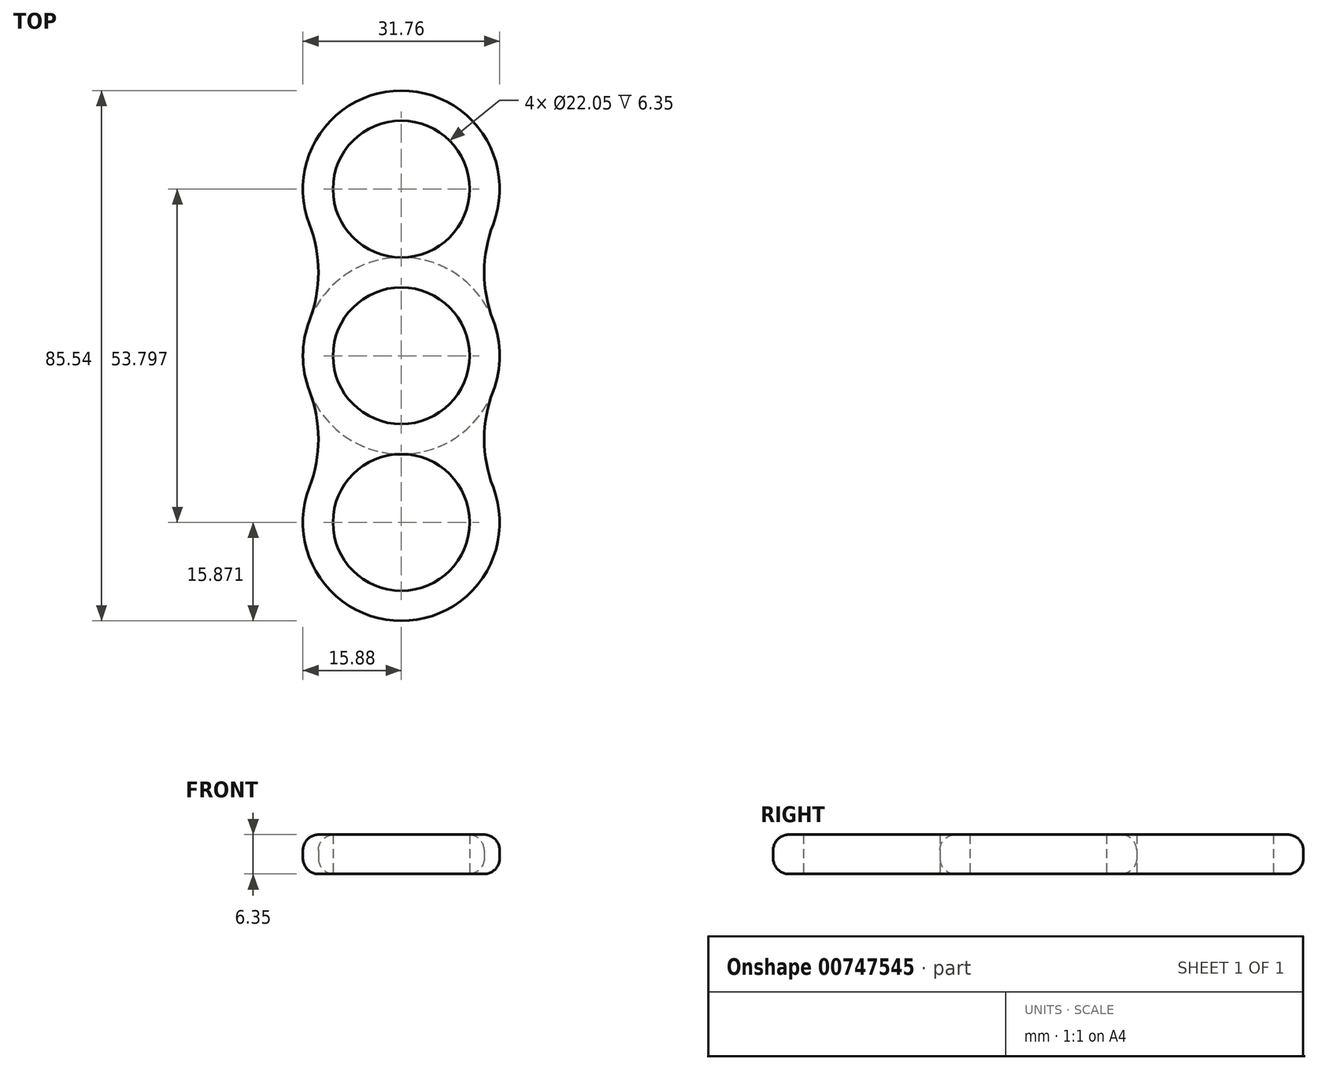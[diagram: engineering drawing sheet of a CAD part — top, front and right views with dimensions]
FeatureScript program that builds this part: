
annotation { "Feature Type Name" : "Feature", "Feature Type Description" : "" }
export const myFeature = defineFeature(function(context is Context, id is Id, definition is map)
    precondition{}
    {
        {
            var Q0;
            Q0=qCreatedBy(makeId("Top.planeOp"),FACE);
            var sketch = newSketch(context, id + "F0", { "sketchPlane" : qUnion([Q0])});
            skCircle(sketch, "E0", {"center": v(0, 0) * mm, "radius": 11.02 * mm});
            skCircle(sketch, "E1", {"center": v(0, 0) * mm, "radius": 15.88 * mm});
            skCircle(sketch, "E2", {"center": v(0, 26.9) * mm, "radius": 11.02 * mm});
            skCircle(sketch, "E3", {"center": v(0, 26.9) * mm, "radius": 15.88 * mm});
            skLineSegment(sketch, "E4", {"start": v(0, 26.9) * mm, "end": v(15.88, 26.9) * mm});
            skLineSegment(sketch, "E5", {"start": v(0, 0) * mm, "end": v(15.88, 0) * mm});
            skLineSegment(sketch, "E6", {"start": v(15.88, 0) * mm, "end": v(15.88, 26.9) * mm});
            skLineSegment(sketch, "E7", {"start": v(0, 0) * mm, "end": v(-15.88, 0) * mm});
            skLineSegment(sketch, "E8", {"start": v(-15.88, 0) * mm, "end": v(-15.88, 26.9) * mm});
            skLineSegment(sketch, "E9", {"start": v(-15.88, 26.9) * mm, "end": v(0, 26.9) * mm});
            skCircle(sketch, "E10", {"center": v(-34.97, 13.45) * mm, "radius": 21.59 * mm});
            skCircle(sketch, "E11", {"center": v(34.97, 13.45) * mm, "radius": 21.59 * mm});
            skSolve(sketch);
        }
        {
            var Q0;
            {var subQ0=sQuery(id+"F0.wireOp",EDGE,"E9");var subQ1=sQuery(id+"F0.wireOp",EDGE,"E2");var subQ2=makeQuery(id+"F0.imprint","INTERSECT",VERTEX,{"derivedFrom":[subQ1,subQ0]});Q0=makeQuery(id+"F0.imprint","IMPRINT",FACE,{"disambiguationData":[TD([[makeQuery(id+"F0.imprint","IMPRINT",EDGE,{"disambiguationData":[TD([[subQ2,1.0]])],"derivedFrom":subQ1}),-1.0]])]});}
            var Q1;
            {var subQ1=sQuery(id+"F0.wireOp",EDGE,"E3");var subQ4=sQuery(id+"F0.wireOp",EDGE,"E1");var subQ5=makeQuery(id+"F0.imprint","INTERSECT",VERTEX,{"disambiguationData":[OD(0.0)],"derivedFrom":[subQ4,subQ1]});Q1=makeQuery(id+"F0.imprint","IMPRINT",FACE,{"disambiguationData":[TD([[makeQuery(id+"F0.imprint","IMPRINT",EDGE,{"disambiguationData":[TD([[subQ5,-1.0]])],"derivedFrom":subQ4}),-1.0]])]});}
            var Q2;
            {var subQ1=sQuery(id+"F0.wireOp",EDGE,"E1");var subQ6=sQuery(id+"F0.wireOp",EDGE,"E2");var subQ7=makeQuery(id+"F0.imprint","INTERSECT",VERTEX,{"derivedFrom":[subQ1,subQ6]});Q2=makeQuery(id+"F0.imprint","IMPRINT",FACE,{"disambiguationData":[TD([[makeQuery(id+"F0.imprint","IMPRINT",EDGE,{"disambiguationData":[TD([[subQ7,-1.0]])],"derivedFrom":subQ1}),-1.0]])]});}
            var Q3;
            {var subQ0=sQuery(id+"F0.wireOp",EDGE,"E3");var subQ1=sQuery(id+"F0.wireOp",EDGE,"E1");var subQ2=makeQuery(id+"F0.imprint","INTERSECT",VERTEX,{"disambiguationData":[OD(0.0)],"derivedFrom":[subQ1,subQ0]});Q3=makeQuery(id+"F0.imprint","IMPRINT",FACE,{"disambiguationData":[TD([[makeQuery(id+"F0.imprint","IMPRINT",EDGE,{"disambiguationData":[TD([[subQ2,-1.0]])],"derivedFrom":subQ1}),1.0]])]});}
            var Q4;
            {var subQ0=sQuery(id+"F0.wireOp",EDGE,"E3");var subQ1=sQuery(id+"F0.wireOp",EDGE,"E0");var subQ2=makeQuery(id+"F0.imprint","INTERSECT",VERTEX,{"derivedFrom":[subQ1,subQ0]});Q4=makeQuery(id+"F0.imprint","IMPRINT",FACE,{"disambiguationData":[TD([[makeQuery(id+"F0.imprint","IMPRINT",EDGE,{"disambiguationData":[TD([[subQ2,1.0]])],"derivedFrom":subQ1}),-1.0]])]});}
            var Q5;
            {var subQ4=sQuery(id+"F0.wireOp",EDGE,"E3");var subQ6=sQuery(id+"F0.wireOp",EDGE,"E0");var subQ7=makeQuery(id+"F0.imprint","INTERSECT",VERTEX,{"derivedFrom":[subQ6,subQ4]});Q5=makeQuery(id+"F0.imprint","IMPRINT",FACE,{"disambiguationData":[TD([[makeQuery(id+"F0.imprint","IMPRINT",EDGE,{"disambiguationData":[TD([[subQ7,-1.0]])],"derivedFrom":subQ6}),-1.0]])]});}
            var Q6;
            {var subQ0=sQuery(id+"F0.wireOp",EDGE,"E5");var subQ1=sQuery(id+"F0.wireOp",EDGE,"E0");var subQ2=makeQuery(id+"F0.imprint","INTERSECT",VERTEX,{"derivedFrom":[subQ1,subQ0]});Q6=makeQuery(id+"F0.imprint","IMPRINT",FACE,{"disambiguationData":[TD([[makeQuery(id+"F0.imprint","IMPRINT",EDGE,{"disambiguationData":[TD([[subQ2,1.0]])],"derivedFrom":subQ1}),-1.0]])]});}
            var Q7;
            {var subQ0=sQuery(id+"F0.wireOp",EDGE,"E11");var subQ1=sQuery(id+"F0.wireOp",EDGE,"E1");var subQ2=makeQuery(id+"F0.imprint","INTERSECT",VERTEX,{"derivedFrom":[subQ1,subQ0]});Q7=makeQuery(id+"F0.imprint","IMPRINT",FACE,{"disambiguationData":[TD([[makeQuery(id+"F0.imprint","IMPRINT",EDGE,{"disambiguationData":[TD([[subQ2,-1.0]])],"derivedFrom":subQ1}),-1.0]])]});}
            var Q8;
            {var subQ0=sQuery(id+"F0.wireOp",EDGE,"E3");var subQ1=sQuery(id+"F0.wireOp",EDGE,"E1");var subQ2=makeQuery(id+"F0.imprint","INTERSECT",VERTEX,{"disambiguationData":[OD(1.0)],"derivedFrom":[subQ1,subQ0]});Q8=makeQuery(id+"F0.imprint","IMPRINT",FACE,{"disambiguationData":[TD([[makeQuery(id+"F0.imprint","IMPRINT",EDGE,{"disambiguationData":[TD([[subQ2,-1.0]])],"derivedFrom":subQ1}),-1.0]])]});}
            extrude(context, id + "F1", {"entities" : qUnion([Q0, Q1, Q2, Q3, Q4, Q5, Q6, Q7, Q8]), "depth" : 6.35 * mm, "offsetDistance" : 25.4 * mm});
        }
        {
            var Q0;
            Q0=qCreatedBy(makeId("Top.planeOp"),FACE);
            var sketch = newSketch(context, id + "F2", { "sketchPlane" : qUnion([Q0])});
            skCircle(sketch, "E12", {"center": v(0, 0) * mm, "radius": 6.5 * mm});
            skSolve(sketch);
        }
        {
            var Q0;
            Q0=makeQuery(id+"F1.opExtrude","SWEPT_BODY",BODY,{"disambiguationData":[OSD([sQuery(id+"F0.wireOp",EDGE,"E0"),sQuery(id+"F0.wireOp",EDGE,"E1"),sQuery(id+"F0.wireOp",EDGE,"E2"),sQuery(id+"F0.wireOp",EDGE,"E3"),sQuery(id+"F0.wireOp",EDGE,"E10"),sQuery(id+"F0.wireOp",EDGE,"E11")])]});
            var Q1;
            Q1=sQuery(id+"F2.wireOp",EDGE,"E12");
            circularPattern(context, id + "F3", {"entities" : qUnion([Q0]), "axis" : qUnion([Q1]), "angle" : 360 * degree, "instanceCount" : 2, "equalSpace" : true});
        }
        {
            var Q0;
            Q0=makeQuery(id+"F1.opExtrude","CAP_EDGE",EDGE,{"disambiguationData":[OSD([sQuery(id+"F0.wireOp",EDGE,"E3")])],"isStart":false});
            var Q1;
            Q1=makeQuery(id+"F3.opPattern","COPY",EDGE,{"derivedFrom":makeQuery(id+"F1.opExtrude","CAP_EDGE",EDGE,{"disambiguationData":[OSD([sQuery(id+"F0.wireOp",EDGE,"E3")])],"isStart":false}),"instanceName":"1"});
            var Q2;
            Q2=makeQuery(id+"F3.opPattern","COPY",FACE,{"derivedFrom":makeQuery(id+"F1.opExtrude","SWEPT_FACE",FACE,{"disambiguationData":[OSD([sQuery(id+"F0.wireOp",EDGE,"E3")])]}),"instanceName":"1"});
            var Q3;
            Q3=makeQuery(id+"F1.opExtrude","CAP_EDGE",EDGE,{"disambiguationData":[OSD([sQuery(id+"F0.wireOp",EDGE,"E3")])],"isStart":true});
            fillet(context, id + "F4", {"entities" : qUnion([Q0, Q1, Q2, Q3]), "radius" : 2.54 * mm, "tangentPropagation" : true, "allowEdgeOverflow" : false});
        }
    });
